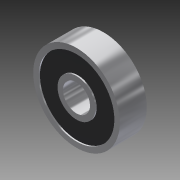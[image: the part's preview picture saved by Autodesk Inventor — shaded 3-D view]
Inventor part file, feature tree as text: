
AUTODESK INVENTOR PART (.ipt)
format: ipt  version: 2014 SP1 (Build 180222100, 222)  size: 116,736 bytes
history: native  units: in
note: dims shown in document units (in); Inventor stores cm internally (conversion verified against a paired STEP export)
features: revolve x1, sketch x1
ambient origin geometry x8: Origin, YZ Plane, XZ Plane, XY Plane, X Axis, Y Axis, Z Axis, Center Point
bodies: Solid1 (feature_tree)
feature tree (2):
  revolve  "Revolution1"  [1 undecoded]
  sketch  "Sketch1"  dims[d0=0.1969in d1=0.6299in d2=0.0394in d3=0.0394in d4=0.0098in d5=0.0098in d6=0.1969in d7=90.0deg]
note: 1 required parameter value undecoded (feature->parameter linkage not recoverable at this tier; creation-order binding heuristic only, values carry confidence <= 0.55)
